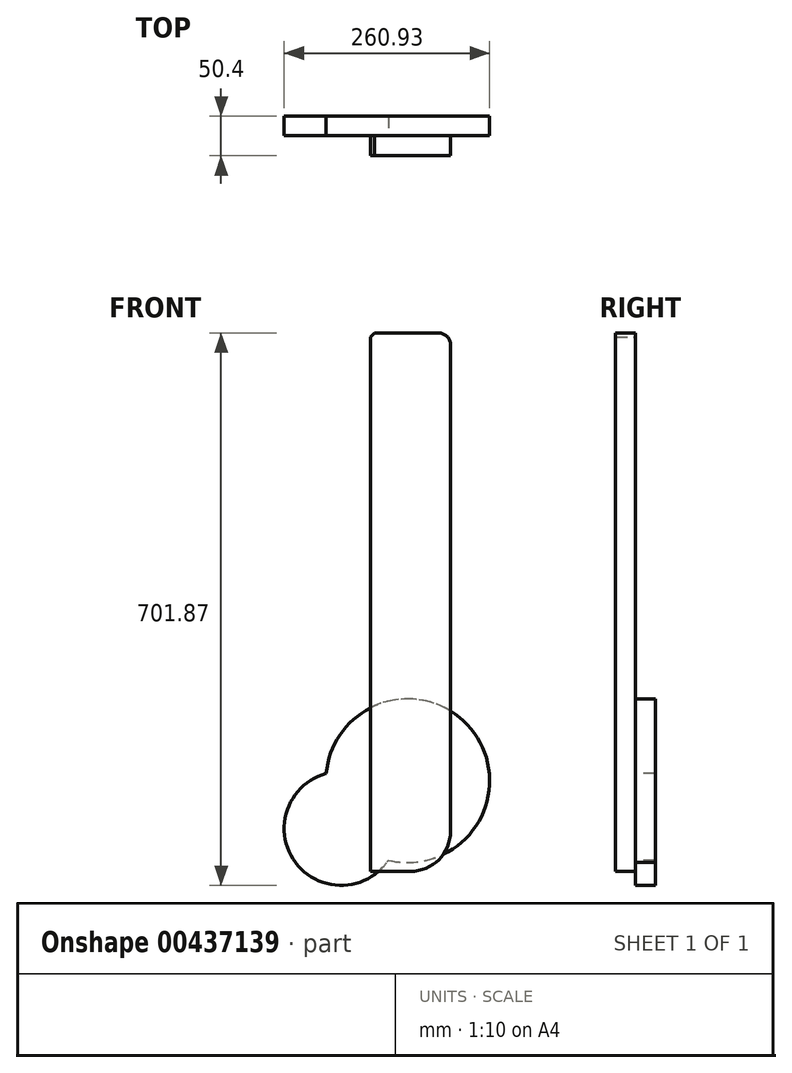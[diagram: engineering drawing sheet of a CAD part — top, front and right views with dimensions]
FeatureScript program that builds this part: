
annotation { "Feature Type Name" : "Feature", "Feature Type Description" : "" }
export const myFeature = defineFeature(function(context is Context, id is Id, definition is map)
    precondition{}
    {
        {
            var Q0;
            Q0=qCreatedBy(makeId("Front.planeOp"),FACE);
            var sketch = newSketch(context, id + "F0", { "sketchPlane" : qUnion([Q0])});
            skLineSegment(sketch, "E0.bottom", {"start": v(-50.86, 342.06) * mm, "end": v(50.86, 342.06) * mm});
            skLineSegment(sketch, "E0.top", {"start": v(-50.86, -342.06) * mm, "end": v(0.06, -342.06) * mm});
            skLineSegment(sketch, "E0.left", {"start": v(-50.86, 342.06) * mm, "end": v(-50.86, -342.06) * mm});
            skLineSegment(sketch, "E0.right", {"start": v(50.86, 342.06) * mm, "end": v(50.86, -291.26) * mm});
            skPoint(sketch, "E0.middle", {"position": v(0, 0) * mm});
            skPoint(sketch, "E1.visualSharp", {"position": v(50.86, -342.06) * mm});
            skArc(sketch, "E1.filletArc", {"start": v(0.06, -342.06) * mm, "mid": v(35.98, -327.18) * mm, "end": v(50.86, -291.26) * mm});
            skSolve(sketch);
        }
        {
            var Q0;
            Q0 = qSketchRegion(id + "F0", true);
            extrude(context, id + "F1", {"entities" : qUnion([Q0]), "depth" : 25.4 * mm});
        }
        {
            var Q0;
            Q0=makeQuery(id+"F1.opExtrude","SWEPT_EDGE",EDGE,{"disambiguationData":[OSD([sQuery(id+"F0.wireOp",EDGE,"E0.bottom"),sQuery(id+"F0.wireOp",EDGE,"E0.left")])]});
            chamfer(context, id + "F2", {"entities" : qUnion([Q0]), "width" : 5.08 * mm, "tangentPropagation" : true});
        }
        {
            var Q0;
            Q0=makeQuery(id+"F1.opExtrude","SWEPT_EDGE",EDGE,{"disambiguationData":[OSD([sQuery(id+"F0.wireOp",EDGE,"E0.bottom"),sQuery(id+"F0.wireOp",EDGE,"E0.right")])]});
            fillet(context, id + "F3", {"entities" : qUnion([Q0]), "radius" : 15.28 * mm, "tangentPropagation" : true, "allowEdgeOverflow" : false});
        }
        {
            var Q0;
            Q0=makeQuery(id+"F1.opExtrude","CAP_FACE",FACE,{"disambiguationData":[OSD([sQuery(id+"F0.wireOp",EDGE,"E0.bottom"),sQuery(id+"F0.wireOp",EDGE,"E0.top"),sQuery(id+"F0.wireOp",EDGE,"E0.left"),sQuery(id+"F0.wireOp",EDGE,"E0.right"),sQuery(id+"F0.wireOp",EDGE,"E1.filletArc")])],"isStart":true});
            var sketch = newSketch(context, id + "F4", { "sketchPlane" : qUnion([Q0])});
            skCircle(sketch, "E2", {"center": v(88, -287.4) * mm, "radius": 72.4 * mm});
            skCircle(sketch, "E3", {"center": v(3.46, -226.86) * mm, "radius": 103.99 * mm});
            skCircle(sketch, "E4", {"center": v(3.46, -226.86) * mm, "radius": 124.58 * mm, "construction": true});
            skSolve(sketch);
        }
        {
            var Q0;
            Q0 = qSketchRegion(id + "F4", true);
            extrude(context, id + "F5", {"entities" : qUnion([Q0]), "operationType" : NewBodyOperationType.ADD, "depth" : 25 * mm});
        }
    });
